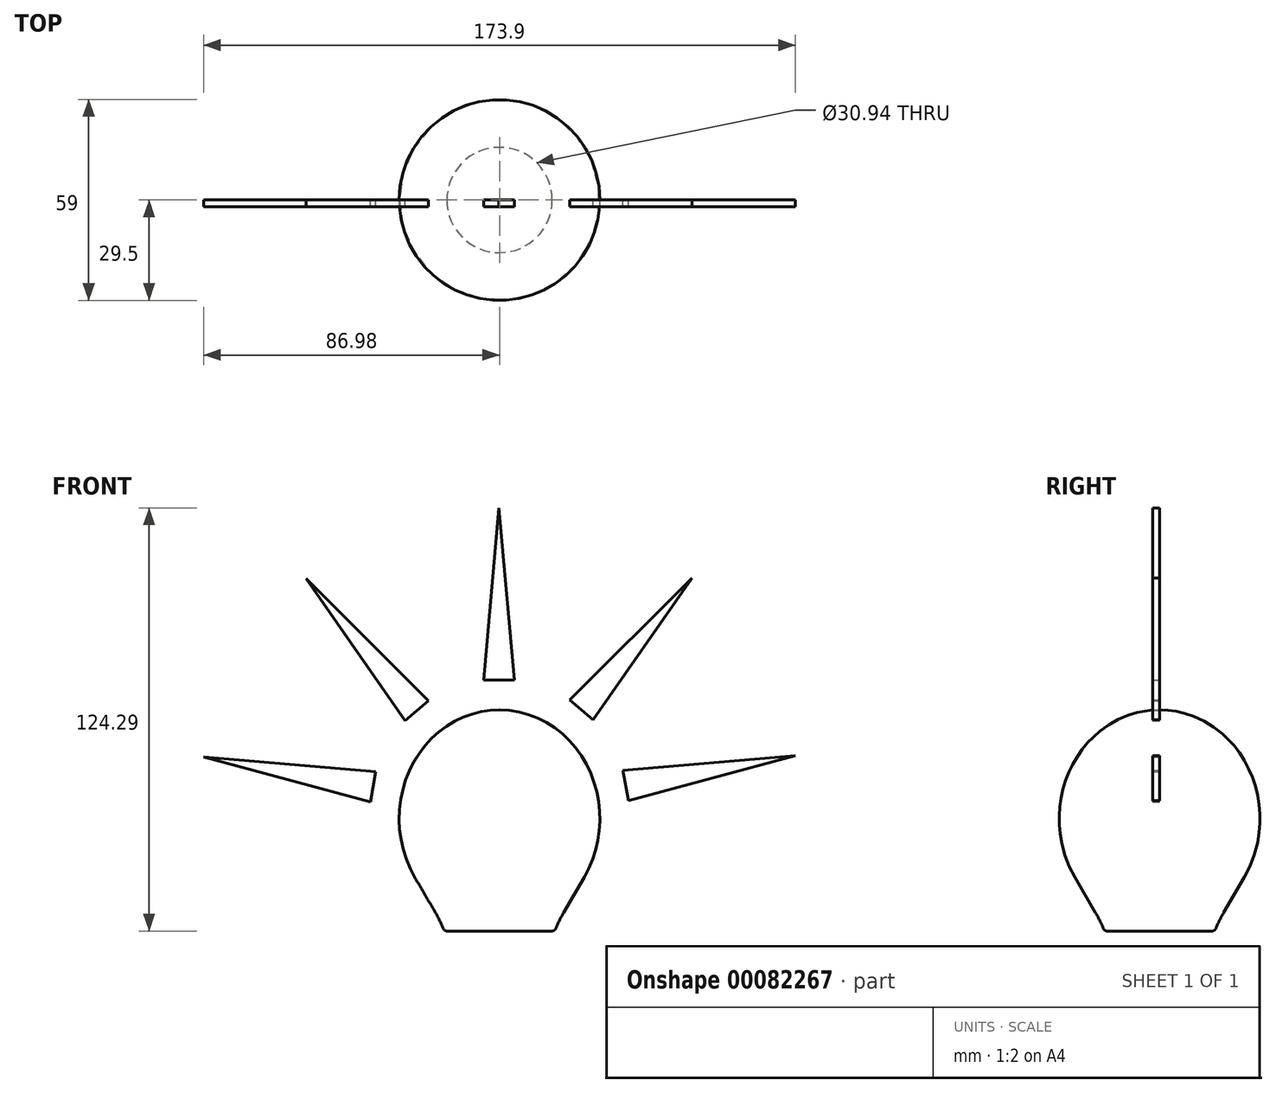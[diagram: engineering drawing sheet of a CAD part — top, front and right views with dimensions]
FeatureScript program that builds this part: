
annotation { "Feature Type Name" : "Feature", "Feature Type Description" : "" }
export const myFeature = defineFeature(function(context is Context, id is Id, definition is map)
    precondition{}
    {
        {
            var Q0;
            Q0=qCreatedBy(makeId("Front.planeOp"),FACE);
            var sketch = newSketch(context, id + "F0", { "sketchPlane" : qUnion([Q0])});
            skLineSegment(sketch, "E0", {"start": v(0, 0) * mm, "end": v(0, 65) * mm});
            skPoint(sketch, "E1", {"position": v(0, 32.5) * mm});
            skPoint(sketch, "E2.orphan", {"position": v(-21.04, 26.04) * mm});
            skPoint(sketch, "E3.orphan", {"position": v(-21.04, 0) * mm});
            skLineSegment(sketch, "E4", {"start": v(-15.47, 0) * mm, "end": v(0, 0) * mm});
            skPoint(sketch, "E5.second.point", {"position": v(0, 8.98) * mm});
            skPoint(sketch, "E5.third.point", {"position": v(-24.57, 58.48) * mm});
            skEllipticalArc(sketch, "E6", {});
            skPoint(sketch, "E7.orphan", {"position": v(-21.04, 14.06) * mm});
            skLineSegment(sketch, "E8", {"start": v(-24.92, 15.83) * mm, "end": v(-18.87, 5.47) * mm});
            skPoint(sketch, "E9.visualSharp", {"position": v(-20.34, 7.97) * mm});
            skArc(sketch, "E9.filletArc", {"start": v(-16.5, 0.69) * mm, "mid": v(-17.6, 3.12) * mm, "end": v(-18.87, 5.47) * mm});
            skPoint(sketch, "E10.visualSharp", {"position": v(-16, 0) * mm});
            skArc(sketch, "E10.filletArc", {"start": v(-16.5, 0.69) * mm, "mid": v(-16.09, 0.19) * mm, "end": v(-15.47, 0) * mm});
            const initialGuessF0  = {"E6": [0, 0.03297137370965459, 0, 1, 0.03202862629034541, 0.0295, 0, 2.1355146130499993]};
            skSetInitialGuess(sketch, initialGuessF0);
            skSolve(sketch);
        }
        {
            var Q0;
            Q0=qSketchRegion(id+"F0",true);
            var Q1;
            Q1=sQuery(id+"F0.wireOp",EDGE,"E0");
            revolve(context, id + "F1", {"entities" : qUnion([Q0]), "axis" : qUnion([Q1]), "revolveType" : RevolveType.FULL});
        }
        {
            var Q0;
            Q0=makeQuery(id+"F1.opRevolve","SWEPT_FACE",FACE,{"disambiguationData":[OSD([sQuery(id+"F0.wireOp",EDGE,"E4")])]});
            shell(context, id + "F2", {"entities" : qUnion([Q0]), "thickness" : 0.1 * mm});
        }
        {
            var Q0;
            Q0=qCreatedBy(makeId("Front.planeOp"),FACE);
            var sketch = newSketch(context, id + "F3", { "sketchPlane" : qUnion([Q0])});
            skLineSegment(sketch, "E11", {"start": v(-0.17, -46.52) * mm, "end": v(-0.17, 124.29) * mm, "construction": true});
            skLineSegment(sketch, "E12", {"start": v(-0.17, 124.29) * mm, "end": v(-4.69, 73.7) * mm});
            skLineSegment(sketch, "E13.MirrorCS", {"start": v(-0.17, 124.29) * mm, "end": v(4.34, 73.7) * mm});
            skLineSegment(sketch, "E14", {"start": v(-4.69, 73.7) * mm, "end": v(4.34, 73.7) * mm});
            skSolve(sketch);
        }
        {
            var Q0;
            Q0 = qSketchRegion(id + "F3", true);
            extrude(context, id + "F4", {"entities" : qUnion([Q0]), "depth" : 2 * mm});
        }
        {
            var Q0;
            Q0=qCreatedBy(makeId("Front.planeOp"),FACE);
            var sketch = newSketch(context, id + "F5", { "sketchPlane" : qUnion([Q0])});
            skCircle(sketch, "E15", {"center": v(0, 36) * mm, "radius": 38.35 * mm, "construction": true});
            skSolve(sketch);
        }
        {
            var Q0;
            Q0=makeQuery(id+"F4.opExtrude","SWEPT_BODY",BODY,{"disambiguationData":[OSD([sQuery(id+"F3.wireOp",EDGE,"E12"),sQuery(id+"F3.wireOp",EDGE,"E13.MirrorCS"),sQuery(id+"F3.wireOp",EDGE,"E14")])]});
            var Q1;
            Q1=sQuery(id+"F5.wireOp",EDGE,"E15");
            circularPattern(context, id + "F6", {"entities" : qUnion([Q0]), "axis" : qUnion([Q1]), "angle" : 40 * degree, "instanceCount" : 3, "oppositeDirection" : true});
        }
        {
            var Q0;
            Q0=makeQuery(id+"F4.opExtrude","SWEPT_BODY",BODY,{"disambiguationData":[OSD([sQuery(id+"F3.wireOp",EDGE,"E12"),sQuery(id+"F3.wireOp",EDGE,"E13.MirrorCS"),sQuery(id+"F3.wireOp",EDGE,"E14")])]});
            var Q1;
            Q1=sQuery(id+"F5.wireOp",EDGE,"E15");
            circularPattern(context, id + "F7", {"entities" : qUnion([Q0]), "axis" : qUnion([Q1]), "angle" : 40 * degree, "instanceCount" : 3});
        }
    });
